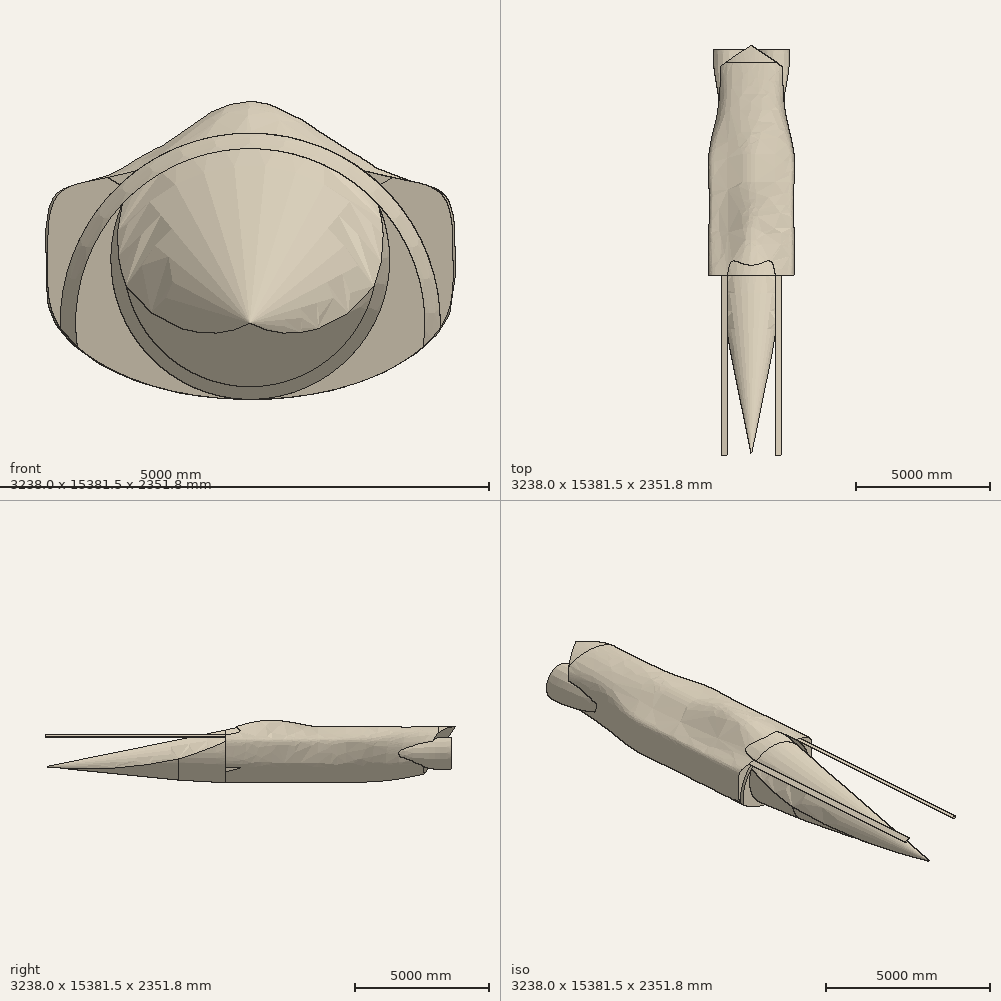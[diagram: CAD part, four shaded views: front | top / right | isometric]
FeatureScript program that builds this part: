
annotation { "Feature Type Name" : "Feature", "Feature Type Description" : "" }
export const myFeature = defineFeature(function(context is Context, id is Id, definition is map)
    precondition{}
    {
        {
            var Q0;
            Q0=qCreatedBy(makeId("Front.planeOp"),FACE);
            cPlane(context, id + "F0", {"entities" : qUnion([Q0]), "cplaneType" : CPlaneType.OFFSET, "offset" : 1750 * mm, "width" : 152.4 * mm, "height" : 152.4 * mm});
        }
        {
            var Q0;
            Q0=qCreatedBy(id+"F0.planeOp",FACE);
            var sketch = newSketch(context, id + "F1", { "sketchPlane" : qUnion([Q0])});
            skPoint(sketch, "E0.middle", {"position": v(0, 0) * mm});
            skFitSpline(sketch, "E1", {"points": [v(0, 877.87) * mm, v(1060, 662.5) * mm, v(1517.6, 506.84) * mm, v(1600, 0) * mm, v(1517.6, -506.84) * mm, v(750, -1000) * mm, v(-750, -1000) * mm, v(-1517.6, -506.84) * mm, v(-1600, 0) * mm, v(-1517.6, 506.84) * mm, v(-1060, 662.5) * mm, v(0, 877.87) * mm]});
            skSolve(sketch);
        }
        {
            var Q0;
            Q0=qCreatedBy(makeId("Front.planeOp"),FACE);
            var sketch = newSketch(context, id + "F2", { "sketchPlane" : qUnion([Q0])});
            skPoint(sketch, "E2.middle", {"position": v(0, 0) * mm});
            skFitSpline(sketch, "E3", {"points": [v(0, 1250) * mm, v(1060, 662.5) * mm, v(1517.6, 506.84) * mm, v(1600, 0) * mm, v(1517.6, -506.84) * mm, v(750, -1000) * mm, v(-750, -1000) * mm, v(-1517.6, -506.84) * mm, v(-1600, 0) * mm, v(-1517.6, 506.84) * mm, v(-1060, 662.5) * mm, v(0, 1250) * mm]});
            skSolve(sketch);
        }
        {
            var Q0;
            Q0=qCreatedBy(makeId("Front.planeOp"),FACE);
            cPlane(context, id + "F3", {"entities" : qUnion([Q0]), "cplaneType" : CPlaneType.OFFSET, "offset" : 1750 * mm, "oppositeDirection" : true, "width" : 150 * mm, "height" : 150 * mm});
        }
        {
            var Q0;
            Q0=qCreatedBy(id+"F3.planeOp",FACE);
            var sketch = newSketch(context, id + "F4", { "sketchPlane" : qUnion([Q0])});
            skPoint(sketch, "E4.middle", {"position": v(0, 0) * mm});
            skFitSpline(sketch, "E5", {"points": [v(0, 1000) * mm, v(1060, 662.5) * mm, v(1517.6, 506.84) * mm, v(1600, 0) * mm, v(1517.6, -506.84) * mm, v(750, -1000) * mm, v(-750, -1000) * mm, v(-1517.6, -506.84) * mm, v(-1600, 0) * mm, v(-1517.6, 506.84) * mm, v(-1060, 662.5) * mm, v(0, 1000) * mm]});
            skSolve(sketch);
        }
        {
            var Q0;
            Q0=qCreatedBy(makeId("Front.planeOp"),FACE);
            cPlane(context, id + "F5", {"entities" : qUnion([Q0]), "cplaneType" : CPlaneType.OFFSET, "offset" : 2800 * mm, "oppositeDirection" : true, "width" : 150 * mm, "height" : 150 * mm});
        }
        {
            var Q0;
            Q0=qCreatedBy(id+"F5.planeOp",FACE);
            var sketch = newSketch(context, id + "F6", { "sketchPlane" : qUnion([Q0])});
            skPoint(sketch, "E6.middle", {"position": v(0, 0) * mm});
            skFitSpline(sketch, "E7", {"points": [v(0, 1000) * mm, v(1060, 662.5) * mm, v(1517.6, 506.84) * mm, v(1600, 0) * mm, v(1517.6, -506.84) * mm, v(750, -1000) * mm, v(-750, -1000) * mm, v(-1517.6, -506.84) * mm, v(-1600, 0) * mm, v(-1517.6, 506.84) * mm, v(-1060, 662.5) * mm, v(0, 1000) * mm]});
            skSolve(sketch);
        }
        {
            var Q0;
            Q0=qCreatedBy(makeId("Front.planeOp"),FACE);
            cPlane(context, id + "F7", {"entities" : qUnion([Q0]), "cplaneType" : CPlaneType.OFFSET, "offset" : 4500 * mm, "oppositeDirection" : true, "width" : 150 * mm, "height" : 150 * mm});
        }
        {
            var Q0;
            Q0=qCreatedBy(id+"F7.planeOp",FACE);
            var sketch = newSketch(context, id + "F8", { "sketchPlane" : qUnion([Q0])});
            skPoint(sketch, "E8.middle", {"position": v(0, 0) * mm});
            skFitSpline(sketch, "E9", {"points": [v(0, 1000) * mm, v(1060, 662.5) * mm, v(1250, 0) * mm, v(1060, -662.5) * mm, v(0, -1000) * mm, v(-1060, -662.5) * mm, v(-1250, 0) * mm, v(-1060, 662.5) * mm, v(0, 1000) * mm]});
            skSolve(sketch);
        }
        {
            var Q0;
            Q0=qCreatedBy(makeId("Front.planeOp"),FACE);
            cPlane(context, id + "F9", {"entities" : qUnion([Q0]), "cplaneType" : CPlaneType.OFFSET, "offset" : 6232.05 * mm, "oppositeDirection" : true, "width" : 150 * mm, "height" : 150 * mm});
        }
        {
            var Q0;
            Q0=qCreatedBy(id+"F9.planeOp",FACE);
            var sketch = newSketch(context, id + "F10", { "sketchPlane" : qUnion([Q0])});
            skPoint(sketch, "E10.middle", {"position": v(0, 0) * mm});
            skFitSpline(sketch, "E11", {"points": [v(0, 1000) * mm, v(1060, 662.5) * mm, v(1250, 0) * mm, v(848, -530) * mm, v(-848, -530) * mm, v(-1250, 0) * mm, v(-1060, 662.5) * mm, v(0, 1000) * mm]});
            skSolve(sketch);
        }
        {
            var Q0;
            Q0=qSketchRegion(id+"F1",true);
            var Q1;
            Q1=qSketchRegion(id+"F2",true);
            var Q2;
            Q2=qSketchRegion(id+"F4",true);
            var Q3;
            Q3=qSketchRegion(id+"F6",true);
            var Q4;
            Q4=qSketchRegion(id+"F8",true);
            var Q5;
            Q5=qSketchRegion(id+"F10",true);
            loft(context, id + "F11", {"sheetProfilesArray" : [{ "sheetProfileEntities" : qUnion([Q0]) }, { "sheetProfileEntities" : qUnion([Q1]) }, { "sheetProfileEntities" : qUnion([Q2]) }, { "sheetProfileEntities" : qUnion([Q3]) }, { "sheetProfileEntities" : qUnion([Q4]) }, { "sheetProfileEntities" : qUnion([Q5]) }]});
        }
        {
            var Q0;
            Q0=makeQuery(id+"F11.opLoft","CAP_FACE",FACE,{"disambiguationData":[OSD([makeQuery(id+"F10.imprint","IMPRINT",FACE,{"disambiguationData":[TD([[makeQuery(id+"F10.imprint","IMPRINT",EDGE,{"derivedFrom":sQuery(id+"F10.wireOp",EDGE,"E11")}),-1.0]])]})])],"isStart":true});
            extrude(context, id + "F12", {"entities" : qUnion([Q0]), "operationType" : NewBodyOperationType.ADD, "depth" : 649.4 * mm});
        }
        {
            var Q0;
            Q0=qCreatedBy(makeId("Right.planeOp"),FACE);
            var sketch = newSketch(context, id + "F13", { "sketchPlane" : qUnion([Q0])});
            skLineSegment(sketch, "E12", {"start": v(0, 0) * mm, "end": v(4500, 0) * mm});
            skLineSegment(sketch, "E13", {"start": v(4500, 0) * mm, "end": v(6232.05, 0) * mm});
            skLineSegment(sketch, "E14", {"start": v(4500, 0) * mm, "end": v(4500, 1000) * mm});
            skLineSegment(sketch, "E15", {"start": v(4500, 1000) * mm, "end": v(6881.46, 1000) * mm});
            skLineSegment(sketch, "E16", {"start": v(6881.46, 1000) * mm, "end": v(6881.46, -1000) * mm});
            skLineSegment(sketch, "E17", {"start": v(6881.46, 1000) * mm, "end": v(6232.05, 0) * mm});
            skLineSegment(sketch, "E18", {"start": v(6232.05, 0) * mm, "end": v(5582.64, -1000) * mm});
            skLineSegment(sketch, "E19", {"start": v(5582.64, -1000) * mm, "end": v(6881.46, -1000) * mm});
            skSolve(sketch);
        }
        {
            var Q0;
            Q0=makeQuery(id+"F13.imprint","IMPRINT",FACE,{"disambiguationData":[TD([[makeQuery(id+"F13.imprint","IMPRINT",EDGE,{"derivedFrom":sQuery(id+"F13.wireOp",EDGE,"E16")}),-1.0]])]});
            var Q1;
            Q1=sQuery(id+"F13.wireOp",EDGE,"E15");
            revolve(context, id + "F14", {"operationType" : NewBodyOperationType.REMOVE, "entities" : qUnion([Q0]), "axis" : qUnion([Q1]), "revolveType" : RevolveType.SYMMETRIC, "oppositeDirection" : true, "angle" : 182 * degree});
        }
        {
            var Q0;
            Q0=makeQuery(id+"F11.opLoft","CAP_FACE",FACE,{"disambiguationData":[OSD([makeQuery(id+"F1.imprint","IMPRINT",FACE,{"disambiguationData":[TD([[makeQuery(id+"F1.imprint","IMPRINT",EDGE,{"derivedFrom":sQuery(id+"F1.wireOp",EDGE,"E1")}),-1.0]])]})])],"isStart":true});
            extrude(context, id + "F15", {"entities" : qUnion([Q0]), "depth" : 6750 * mm});
        }
        {
            var Q0;
            Q0=qCreatedBy(makeId("Right.planeOp"),FACE);
            var sketch = newSketch(context, id + "F16", { "sketchPlane" : qUnion([Q0])});
            skLineSegment(sketch, "E20", {"start": v(0, 0) * mm, "end": v(-3500, 0) * mm});
            skLineSegment(sketch, "E21", {"start": v(-3500, 0) * mm, "end": v(-3500, -1000) * mm});
            skLineSegment(sketch, "E22", {"start": v(-3500, -1000) * mm, "end": v(-8500, -1000) * mm});
            skLineSegment(sketch, "E23", {"start": v(-8500, -1000) * mm, "end": v(-8500, -499.31) * mm});
            skLineSegment(sketch, "E24", {"start": v(-1151.4, 0) * mm, "end": v(-1151.4, 1000) * mm});
            skLineSegment(sketch, "E25", {"start": v(-1151.4, 1000) * mm, "end": v(-8500, -499.31) * mm});
            skLineSegment(sketch, "E26", {"start": v(-8500, -499.31) * mm, "end": v(-3500, -1000) * mm});
            skLineSegment(sketch, "E27", {"start": v(-1151.4, 1000) * mm, "end": v(-8500, 1000) * mm});
            skLineSegment(sketch, "E28", {"start": v(-8500, 1000) * mm, "end": v(-8500, -499.31) * mm});
            skLineSegment(sketch, "E29", {"start": v(-8500, -1000) * mm, "end": v(-8500, -1750) * mm});
            skLineSegment(sketch, "E30", {"start": v(-8500, -1750) * mm, "end": v(-1750, -1750) * mm});
            skPoint(sketch, "E30.endSnap0", {"position": v(-1750, 0) * mm});
            skLineSegment(sketch, "E31", {"start": v(-1750, 0) * mm, "end": v(-1750, -1099.92) * mm});
            skLineSegment(sketch, "E32", {"start": v(-1750, -1099.92) * mm, "end": v(-3500, -1000) * mm});
            skLineSegment(sketch, "E33", {"start": v(-1750, -1099.92) * mm, "end": v(-1750, -1750) * mm});
            skLineSegment(sketch, "E34", {"start": v(-8500, -499.31) * mm, "end": v(-3500, -499.31) * mm});
            skSolve(sketch);
        }
        {
            var Q0;
            Q0=makeQuery(id+"F16.imprint","IMPRINT",FACE,{"disambiguationData":[TD([[makeQuery(id+"F16.imprint","IMPRINT",EDGE,{"derivedFrom":sQuery(id+"F16.wireOp",EDGE,"E25")}),-1.0]])]});
            var Q1;
            Q1=sQuery(id+"F16.wireOp",EDGE,"E34");
            revolve(context, id + "F17", {"operationType" : NewBodyOperationType.REMOVE, "entities" : qUnion([Q0]), "axis" : qUnion([Q1]), "revolveType" : RevolveType.SYMMETRIC, "oppositeDirection" : true, "angle" : 250 * degree});
        }
        {
            var Q0;
            Q0=makeQuery(id+"F16.imprint","IMPRINT",FACE,{"disambiguationData":[TD([[makeQuery(id+"F16.imprint","IMPRINT",EDGE,{"derivedFrom":sQuery(id+"F16.wireOp",EDGE,"E22")}),-1.0]])]});
            var Q1;
            Q1=makeQuery(id+"F16.imprint","IMPRINT",FACE,{"disambiguationData":[TD([[makeQuery(id+"F16.imprint","IMPRINT",EDGE,{"derivedFrom":sQuery(id+"F16.wireOp",EDGE,"E22")}),1.0]])]});
            var Q2;
            Q2=sQuery(id+"F16.wireOp",EDGE,"E20");
            revolve(context, id + "F18", {"operationType" : NewBodyOperationType.REMOVE, "entities" : qUnion([Q0, Q1]), "axis" : qUnion([Q2]), "revolveType" : RevolveType.SYMMETRIC, "angle" : 240 * degree});
        }
        {
            var Q0;
            Q0=qCreatedBy(makeId("Front.planeOp"),FACE);
            cPlane(context, id + "F19", {"entities" : qUnion([Q0]), "cplaneType" : CPlaneType.OFFSET, "offset" : 3500 * mm, "oppositeDirection" : true, "width" : 150 * mm, "height" : 150 * mm});
        }
        {
            var Q0;
            Q0=qCreatedBy(id+"F19.planeOp",FACE);
            var sketch = newSketch(context, id + "F20", { "sketchPlane" : qUnion([Q0])});
            skCircle(sketch, "E35", {"center": v(-825, 0) * mm, "radius": 600 * mm});
            skCircle(sketch, "E36", {"center": v(825, 0) * mm, "radius": 600 * mm});
            skSolve(sketch);
        }
        {
            var Q0;
            Q0=qCreatedBy(makeId("Front.planeOp"),FACE);
            cPlane(context, id + "F21", {"entities" : qUnion([Q0]), "cplaneType" : CPlaneType.OFFSET, "offset" : 4500 * mm, "oppositeDirection" : true, "width" : 150 * mm, "height" : 150 * mm});
        }
        {
            var Q0;
            Q0=qCreatedBy(id+"F21.planeOp",FACE);
            var sketch = newSketch(context, id + "F22", { "sketchPlane" : qUnion([Q0])});
            skCircle(sketch, "E37", {"center": v(-825, 0) * mm, "radius": 400 * mm});
            skCircle(sketch, "E38", {"center": v(825, 0) * mm, "radius": 400 * mm});
            skSolve(sketch);
        }
        {
            var Q0;
            Q0=qCreatedBy(makeId("Front.planeOp"),FACE);
            cPlane(context, id + "F23", {"entities" : qUnion([Q0]), "cplaneType" : CPlaneType.OFFSET, "offset" : 6232.05 * mm, "oppositeDirection" : true, "width" : 150 * mm, "height" : 150 * mm});
        }
        {
            var Q0;
            Q0=qCreatedBy(id+"F23.planeOp",FACE);
            var sketch = newSketch(context, id + "F24", { "sketchPlane" : qUnion([Q0])});
            skCircle(sketch, "E39", {"center": v(-825, 0) * mm, "radius": 600 * mm});
            skCircle(sketch, "E40", {"center": v(825, 0) * mm, "radius": 600 * mm});
            skSolve(sketch);
        }
        {
            var Q0;
            Q0=qCreatedBy(makeId("Front.planeOp"),FACE);
            cPlane(context, id + "F25", {"entities" : qUnion([Q0]), "cplaneType" : CPlaneType.OFFSET, "offset" : 6732.05 * mm, "oppositeDirection" : true, "width" : 150 * mm, "height" : 150 * mm});
        }
        {
            var Q0;
            Q0=qCreatedBy(id+"F25.planeOp",FACE);
            var sketch = newSketch(context, id + "F26", { "sketchPlane" : qUnion([Q0])});
            skCircle(sketch, "E41", {"center": v(-825, 0) * mm, "radius": 600 * mm});
            skCircle(sketch, "E42", {"center": v(825, 0) * mm, "radius": 600 * mm});
            skSolve(sketch);
        }
        {
            var Q0;
            Q0=makeQuery(id+"F20.imprint","IMPRINT",FACE,{"disambiguationData":[TD([[makeQuery(id+"F20.imprint","IMPRINT",EDGE,{"derivedFrom":sQuery(id+"F20.wireOp",EDGE,"E35")}),1.0]])]});
            var Q1;
            Q1=makeQuery(id+"F22.imprint","IMPRINT",FACE,{"disambiguationData":[TD([[makeQuery(id+"F22.imprint","IMPRINT",EDGE,{"derivedFrom":sQuery(id+"F22.wireOp",EDGE,"E37")}),1.0]])]});
            var Q2;
            Q2=makeQuery(id+"F24.imprint","IMPRINT",FACE,{"disambiguationData":[TD([[makeQuery(id+"F24.imprint","IMPRINT",EDGE,{"derivedFrom":sQuery(id+"F24.wireOp",EDGE,"E39")}),1.0]])]});
            var Q3;
            Q3=makeQuery(id+"F26.imprint","IMPRINT",FACE,{"disambiguationData":[TD([[makeQuery(id+"F26.imprint","IMPRINT",EDGE,{"derivedFrom":sQuery(id+"F26.wireOp",EDGE,"E41")}),1.0]])]});
            loft(context, id + "F27", {"sheetProfilesArray" : [{ "sheetProfileEntities" : qUnion([Q0]) }, { "sheetProfileEntities" : qUnion([Q1]) }, { "sheetProfileEntities" : qUnion([Q2]) }, { "sheetProfileEntities" : qUnion([Q3]) }]});
        }
        {
            var Q0;
            Q0=makeQuery(id+"F20.imprint","IMPRINT",FACE,{"disambiguationData":[TD([[makeQuery(id+"F20.imprint","IMPRINT",EDGE,{"derivedFrom":sQuery(id+"F20.wireOp",EDGE,"E36")}),1.0]])]});
            var Q1;
            Q1=makeQuery(id+"F22.imprint","IMPRINT",FACE,{"disambiguationData":[TD([[makeQuery(id+"F22.imprint","IMPRINT",EDGE,{"derivedFrom":sQuery(id+"F22.wireOp",EDGE,"E38")}),1.0]])]});
            var Q2;
            Q2=makeQuery(id+"F24.imprint","IMPRINT",FACE,{"disambiguationData":[TD([[makeQuery(id+"F24.imprint","IMPRINT",EDGE,{"derivedFrom":sQuery(id+"F24.wireOp",EDGE,"E40")}),1.0]])]});
            var Q3;
            Q3=makeQuery(id+"F26.imprint","IMPRINT",FACE,{"disambiguationData":[TD([[makeQuery(id+"F26.imprint","IMPRINT",EDGE,{"derivedFrom":sQuery(id+"F26.wireOp",EDGE,"E42")}),1.0]])]});
            loft(context, id + "F28", {"sheetProfilesArray" : [{ "sheetProfileEntities" : qUnion([Q0]) }, { "sheetProfileEntities" : qUnion([Q1]) }, { "sheetProfileEntities" : qUnion([Q2]) }, { "sheetProfileEntities" : qUnion([Q3]) }]});
        }
    });
